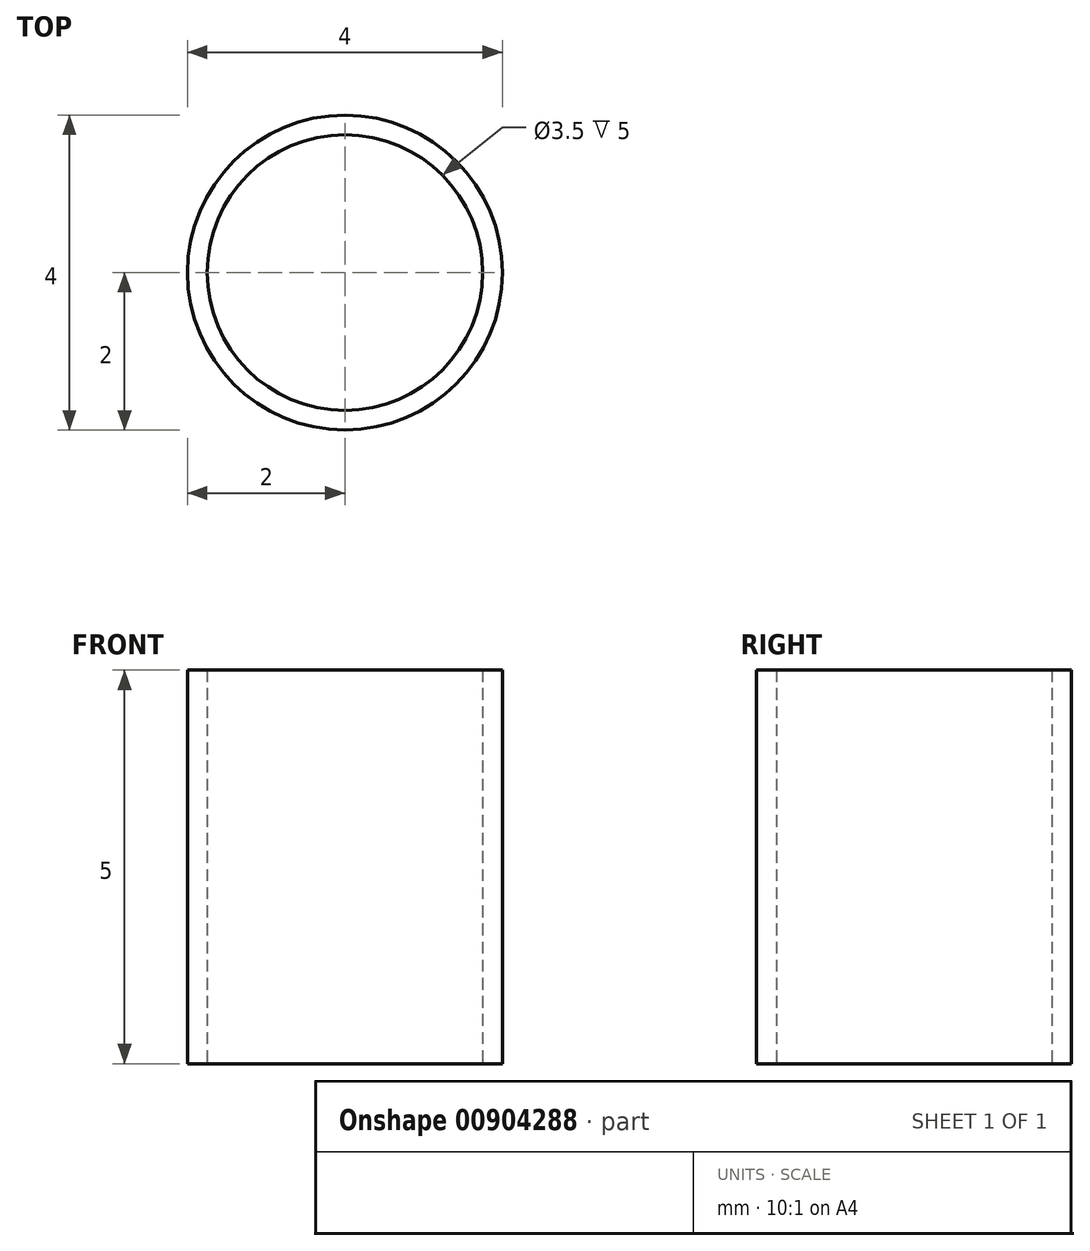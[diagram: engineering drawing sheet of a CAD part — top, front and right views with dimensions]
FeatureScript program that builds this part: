
annotation { "Feature Type Name" : "Feature", "Feature Type Description" : "" }
export const myFeature = defineFeature(function(context is Context, id is Id, definition is map)
    precondition{}
    {
        {
            var Q0;
            Q0=qCreatedBy(makeId("Front.planeOp"),FACE);
            var sketch = newSketch(context, id + "F0", { "sketchPlane" : qUnion([Q0])});
            skLineSegment(sketch, "E0.bottom", {"start": v(0, 0) * mm, "end": v(-1.75, 0) * mm});
            skLineSegment(sketch, "E0.top", {"start": v(0, 5) * mm, "end": v(-1.75, 5) * mm});
            skLineSegment(sketch, "E0.left", {"start": v(0, 0) * mm, "end": v(0, 5) * mm});
            skLineSegment(sketch, "E0.right", {"start": v(-1.75, 0) * mm, "end": v(-1.75, 5) * mm});
            skLineSegment(sketch, "E1.bottom", {"start": v(0, 0) * mm, "end": v(-2, 0) * mm});
            skLineSegment(sketch, "E1.top", {"start": v(0, 5) * mm, "end": v(-2, 5) * mm});
            skLineSegment(sketch, "E1.right", {"start": v(-2, 0) * mm, "end": v(-2, 5) * mm});
            skSolve(sketch);
        }
        {
            var Q0;
            {var subQ0=sQuery(id+"F0.wireOp",EDGE,"E0.right");Q0=makeQuery(id+"F0.imprint","IMPRINT",FACE,{"disambiguationData":[TD([[makeQuery(id+"F0.imprint","IMPRINT",EDGE,{"derivedFrom":subQ0}),1.0]])]});}
            var Q1;
            Q1=sQuery(id+"F0.wireOp",EDGE,"E0.left");
            revolve(context, id + "F1", {"surfaceOperationType" : NewSurfaceOperationType.NEW, "entities" : qUnion([Q0]), "axis" : qUnion([Q1]), "revolveType" : RevolveType.FULL});
        }
    });
